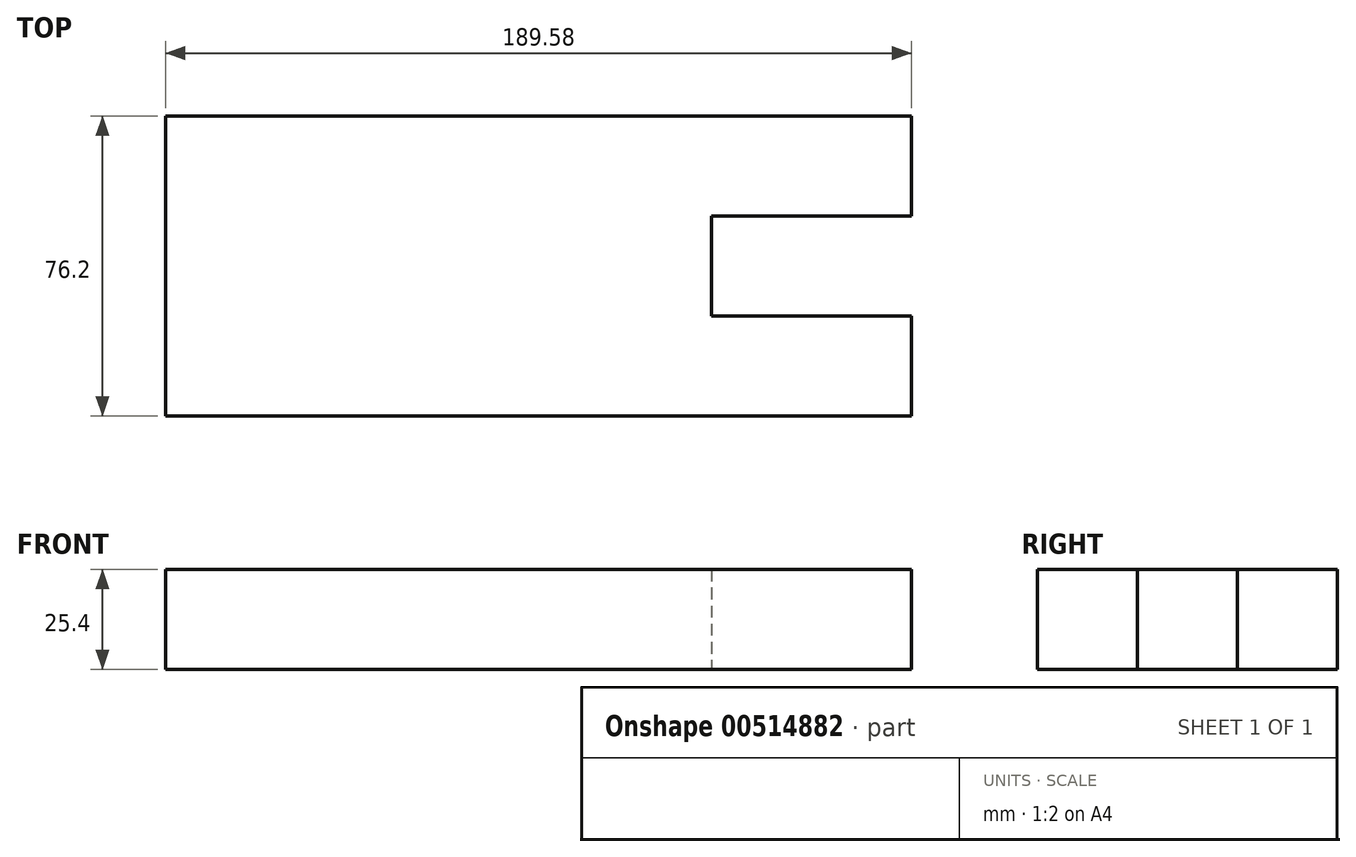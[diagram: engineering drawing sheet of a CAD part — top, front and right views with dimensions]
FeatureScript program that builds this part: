
annotation { "Feature Type Name" : "Feature", "Feature Type Description" : "" }
export const myFeature = defineFeature(function(context is Context, id is Id, definition is map)
    precondition{}
    {
        {
            var Q0;
            Q0=qCreatedBy(makeId("Top.planeOp"),FACE);
            var sketch = newSketch(context, id + "F0", { "sketchPlane" : qUnion([Q0])});
            skLineSegment(sketch, "E0", {"start": v(-89.26, -3.97) * mm, "end": v(-89.26, -80.17) * mm});
            skLineSegment(sketch, "E1", {"start": v(-89.26, -80.17) * mm, "end": v(100.32, -80.17) * mm});
            skLineSegment(sketch, "E2", {"start": v(100.32, -80.17) * mm, "end": v(100.32, -54.77) * mm});
            skLineSegment(sketch, "E3", {"start": v(100.32, -54.77) * mm, "end": v(49.52, -54.77) * mm});
            skLineSegment(sketch, "E4", {"start": v(49.52, -54.77) * mm, "end": v(49.52, -29.37) * mm});
            skLineSegment(sketch, "E5", {"start": v(49.52, -29.37) * mm, "end": v(100.32, -29.37) * mm});
            skLineSegment(sketch, "E6", {"start": v(100.32, -29.37) * mm, "end": v(100.32, -3.97) * mm});
            skLineSegment(sketch, "E7", {"start": v(100.32, -3.97) * mm, "end": v(-89.26, -3.97) * mm});
            skSolve(sketch);
        }
        {
            var Q0;
            Q0 = qSketchRegion(id + "F0", true);
            extrude(context, id + "F1", {"entities" : qUnion([Q0]), "depth" : 25.4 * mm, "offsetDistance" : 25.4 * mm});
        }
    });
